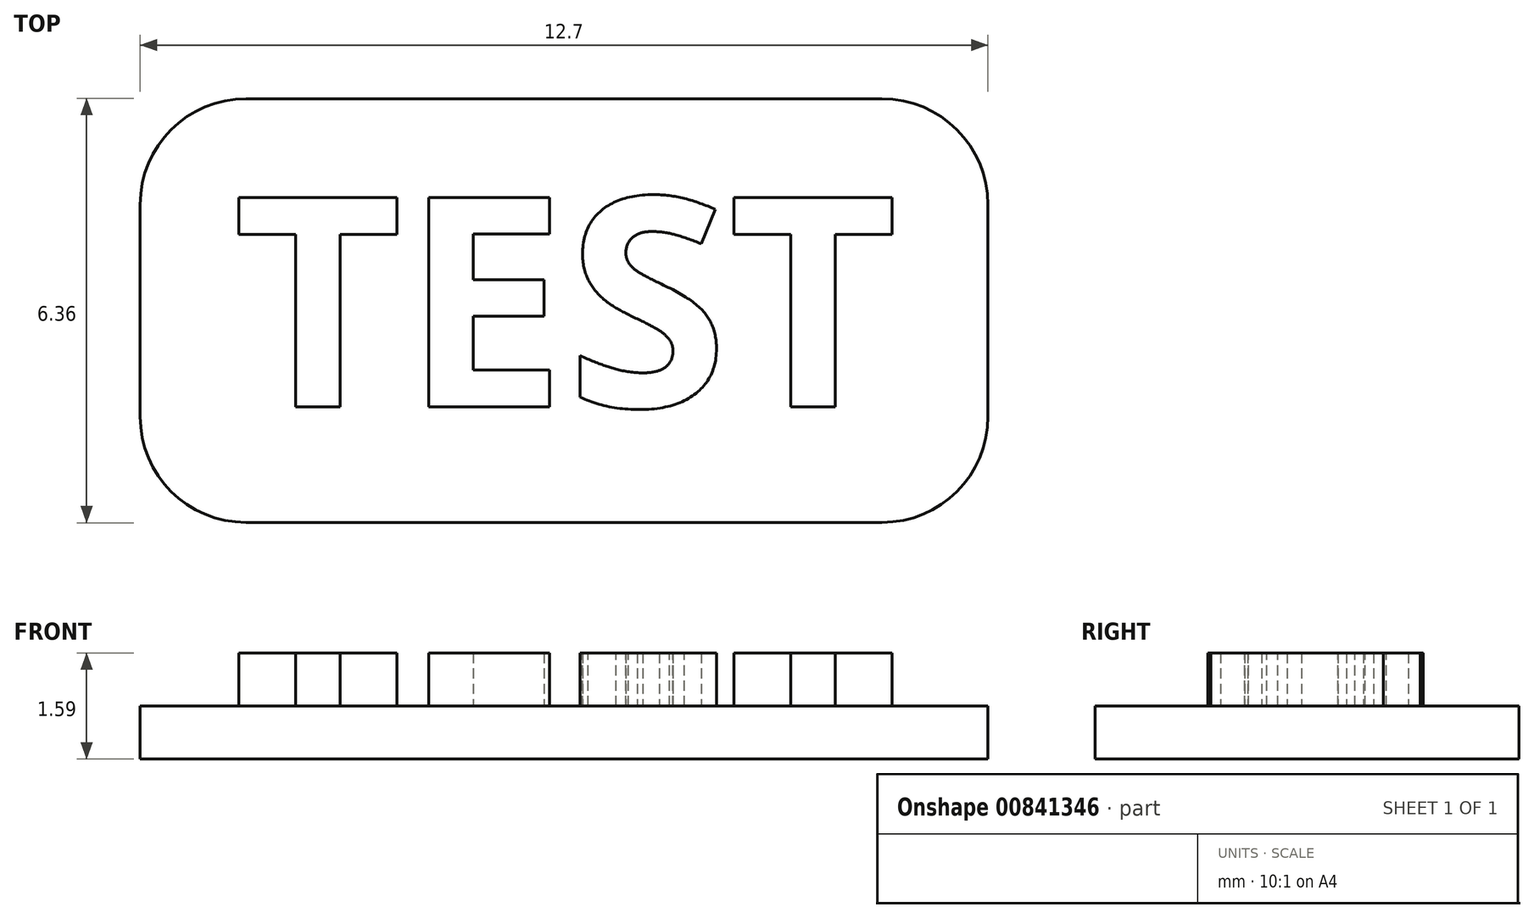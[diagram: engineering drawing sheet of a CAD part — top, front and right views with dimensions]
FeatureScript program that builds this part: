
annotation { "Feature Type Name" : "Feature", "Feature Type Description" : "" }
export const myFeature = defineFeature(function(context is Context, id is Id, definition is map)
    precondition{}
    {
        {
            var Q0;
            Q0=qCreatedBy(makeId("Top.planeOp"),FACE);
            var sketch = newSketch(context, id + "F0", { "sketchPlane" : qUnion([Q0])});
            skLineSegment(sketch, "E0.bottom", {"start": v(6.35, 3.18) * mm, "end": v(-6.35, 3.18) * mm});
            skLineSegment(sketch, "E0.top", {"start": v(6.35, -3.18) * mm, "end": v(-6.35, -3.18) * mm});
            skLineSegment(sketch, "E0.left", {"start": v(6.35, 3.18) * mm, "end": v(6.35, -3.18) * mm});
            skLineSegment(sketch, "E0.right", {"start": v(-6.35, 3.18) * mm, "end": v(-6.35, -3.18) * mm});
            skPoint(sketch, "E0.middle", {"position": v(0, 0) * mm});
            skSolve(sketch);
        }
        {
            var Q0;
            Q0=makeQuery(id+"F0.imprint","IMPRINT",FACE,{"disambiguationData":[TD([[makeQuery(id+"F0.imprint","IMPRINT",EDGE,{"derivedFrom":sQuery(id+"F0.wireOp",EDGE,"E0.bottom")}),1.0]])]});
            extrude(context, id + "F1", {"entities" : qUnion([Q0]), "depth" : 0.8 * mm, "offsetDistance" : 25.4 * mm});
        }
        {
            var Q0;
            Q0=makeQuery(id+"F1.opExtrude","SWEPT_EDGE",EDGE,{"disambiguationData":[OSD([sQuery(id+"F0.wireOp",EDGE,"E0.top"),sQuery(id+"F0.wireOp",EDGE,"E0.right")])]});
            var Q1;
            Q1=makeQuery(id+"F1.opExtrude","SWEPT_EDGE",EDGE,{"disambiguationData":[OSD([sQuery(id+"F0.wireOp",EDGE,"E0.bottom"),sQuery(id+"F0.wireOp",EDGE,"E0.left")])]});
            var Q2;
            Q2=makeQuery(id+"F1.opExtrude","SWEPT_EDGE",EDGE,{"disambiguationData":[OSD([sQuery(id+"F0.wireOp",EDGE,"E0.top"),sQuery(id+"F0.wireOp",EDGE,"E0.left")])]});
            var Q3;
            Q3=makeQuery(id+"F1.opExtrude","SWEPT_EDGE",EDGE,{"disambiguationData":[OSD([sQuery(id+"F0.wireOp",EDGE,"E0.bottom"),sQuery(id+"F0.wireOp",EDGE,"E0.right")])]});
            fillet(context, id + "F2", {"entities" : qUnion([Q0, Q1, Q2, Q3]), "radius" : 1.59 * mm, "tangentPropagation" : true, "allowEdgeOverflow" : false});
        }
        {
            var Q0;
            Q0=makeQuery(id+"F1.opExtrude","CAP_FACE",FACE,{"disambiguationData":[OSD([sQuery(id+"F0.wireOp",EDGE,"E0.bottom"),sQuery(id+"F0.wireOp",EDGE,"E0.top"),sQuery(id+"F0.wireOp",EDGE,"E0.left"),sQuery(id+"F0.wireOp",EDGE,"E0.right")])],"isStart":false});
            var sketch = newSketch(context, id + "F3", { "sketchPlane" : qUnion([Q0])});
            skText(sketch, "E1", { "text": "TEST", "fontName": "OpenSans-Bold.ttf"});
            const initialGuessF3  = {"E1": [-0.00496, -0.00144, 1, 0, 0.00316]};
            skSetInitialGuess(sketch, initialGuessF3);
            skSolve(sketch);
        }
        {
            var Q0;
            Q0=makeQuery(id+"F3.imprint","IMPRINT",FACE,{"disambiguationData":[TD([[makeQuery(id+"F3.imprint","IMPRINT",EDGE,{"derivedFrom":sQuery(id+"F3.wireOp",EDGE,"E1.sketch_text.stroke-0")}),-1.0]])]});
            var Q1;
            Q1=makeQuery(id+"F3.imprint","IMPRINT",FACE,{"disambiguationData":[TD([[makeQuery(id+"F3.imprint","IMPRINT",EDGE,{"derivedFrom":sQuery(id+"F3.wireOp",EDGE,"E1.sketch_text.stroke-8")}),-1.0]])]});
            var Q2;
            Q2=makeQuery(id+"F3.imprint","IMPRINT",FACE,{"disambiguationData":[TD([[makeQuery(id+"F3.imprint","IMPRINT",EDGE,{"derivedFrom":sQuery(id+"F3.wireOp",EDGE,"E1.sketch_text.stroke-20")}),-1.0]])]});
            var Q3;
            Q3=makeQuery(id+"F3.imprint","IMPRINT",FACE,{"disambiguationData":[TD([[makeQuery(id+"F3.imprint","IMPRINT",EDGE,{"derivedFrom":sQuery(id+"F3.wireOp",EDGE,"E1.sketch_text.stroke-45")}),-1.0]])]});
            var Q4;
            Q4=makeQuery(id+"F3.imprint","IMPRINT",FACE,{"disambiguationData":[TD([[makeQuery(id+"F3.imprint","IMPRINT",EDGE,{"derivedFrom":sQuery(id+"F3.wireOp",EDGE,"E1.sketch_text.stroke-48")}),-1.0]])]});
            extrude(context, id + "F4", {"entities" : qUnion([Q0, Q1, Q2, Q3, Q4]), "operationType" : NewBodyOperationType.ADD, "depth" : 0.8 * mm, "offsetDistance" : 25.4 * mm});
        }
    });
